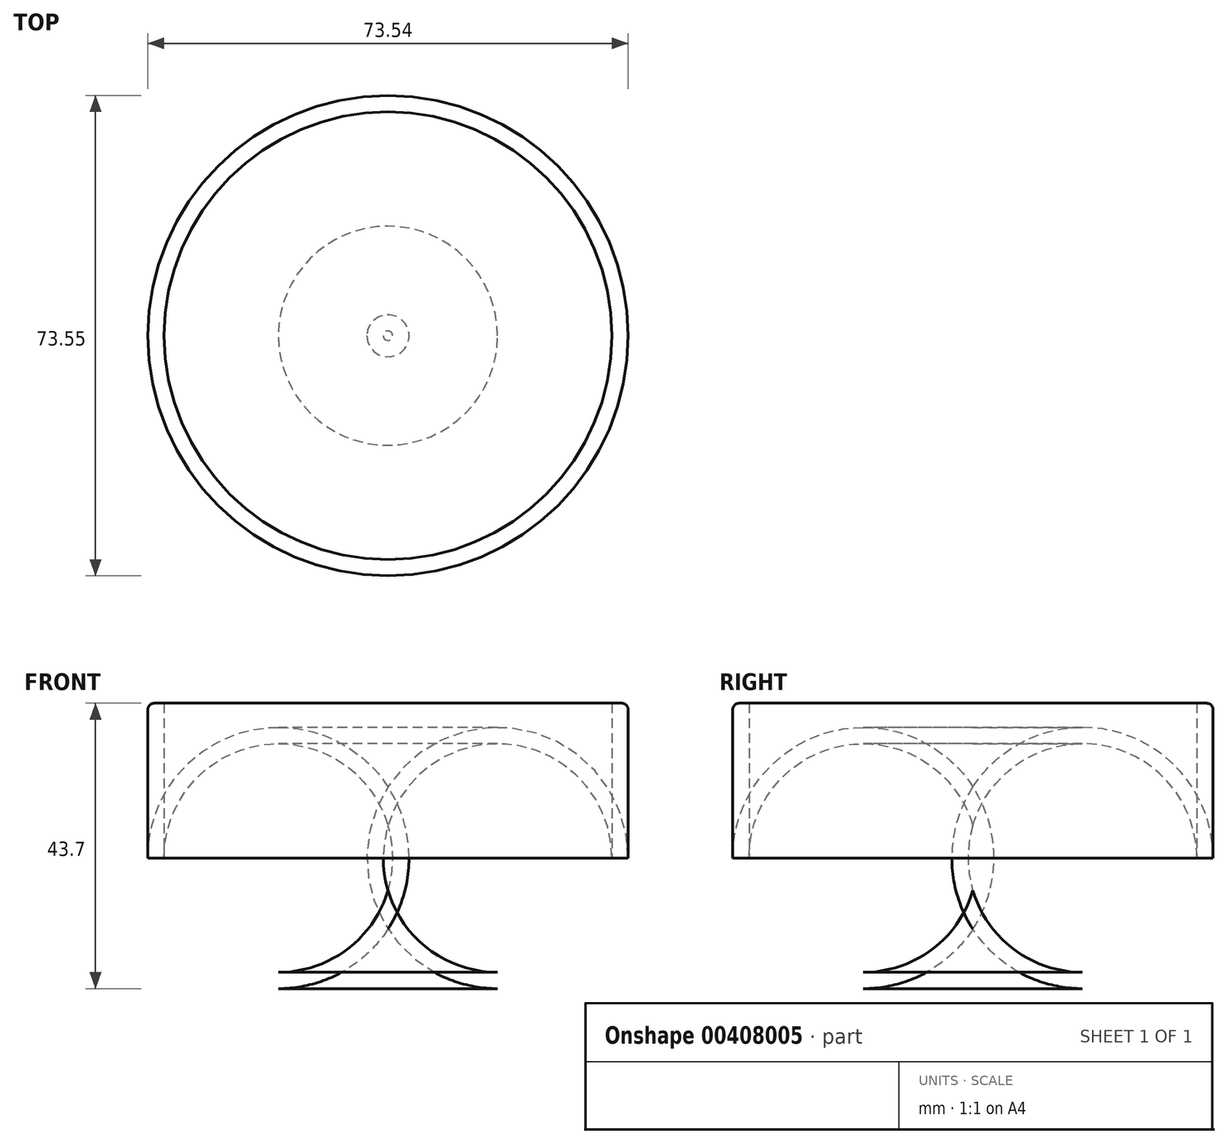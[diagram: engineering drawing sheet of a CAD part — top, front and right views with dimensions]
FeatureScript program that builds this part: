
annotation { "Feature Type Name" : "Feature", "Feature Type Description" : "" }
export const myFeature = defineFeature(function(context is Context, id is Id, definition is map)
    precondition{}
    {
        {
            var Q0;
            Q0=qCreatedBy(makeId("Top.planeOp"),FACE);
            var sketch = newSketch(context, id + "F0", { "sketchPlane" : qUnion([Q0])});
            skCircle(sketch, "E0", {"center": v(-19.62, 28.1) * mm, "radius": 36.77 * mm});
            skSolve(sketch);
        }
        {
            var Q0;
            Q0 = qSketchRegion(id + "F0", true);
            extrude(context, id + "F1", {"entities" : qUnion([Q0]), "depth" : 43.7 * mm});
        }
        {
            var Q0;
            Q0=makeQuery(id+"F1.opExtrude","CAP_EDGE",EDGE,{"disambiguationData":[OSD([sQuery(id+"F0.wireOp",EDGE,"E0")])],"isStart":false});
            fillet(context, id + "F2", {"entities" : qUnion([Q0]), "radius" : 1 * mm, "tangentPropagation" : true, "allowEdgeOverflow" : false});
        }
        {
            var Q0;
            Q0=makeQuery(id+"F1.opExtrude","CAP_EDGE",EDGE,{"disambiguationData":[OSD([sQuery(id+"F0.wireOp",EDGE,"E0")])],"isStart":true});
            fillet(context, id + "F3", {"entities" : qUnion([Q0]), "radius" : 20 * mm, "tangentPropagation" : true, "allowEdgeOverflow" : false});
        }
        {
            var Q0;
            Q0=makeQuery(id+"F1.opExtrude","CAP_FACE",FACE,{"disambiguationData":[OSD([sQuery(id+"F0.wireOp",EDGE,"E0")])],"isStart":false});
            shell(context, id + "F4", {"entities" : qUnion([Q0]), "thickness" : 2.5 * mm});
        }
    });
